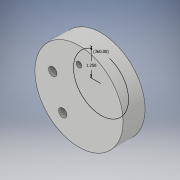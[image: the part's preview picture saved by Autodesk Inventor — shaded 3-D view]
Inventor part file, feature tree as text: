
AUTODESK INVENTOR PART (.ipt)
format: ipt  version: 2018 (Build 220112000, 112)  size: 127,488 bytes
history: native  units: in
note: dims shown in document units (in); Inventor stores cm internally (conversion verified against a paired STEP export)
features: hole x4, sketch x2, extrude x1
ambient origin geometry x8: Origin, YZ Plane, XZ Plane, XY Plane, X Axis, Y Axis, Z Axis, Center Point
bodies: Body1 (feature_tree)
feature tree (7):
  extrude  "Extrusion2"  Depth=2.5in
  sketch  "Sketch4"  dims[d9=1.0in d10=0.0in d12=1.25in d13=1.9685in d15=360.0deg d17=0.25in d18=0.75in d19=0.375in d20=0.25in d21=0.5635in d22=1.25in d23=0.8108in d24=0.375in d25=0.75in d26=0.75in d27=0.25in d28=0.5635in d29=1.25in d30=0.8108in d31=0.196in d32=0.5in d33=0.375in d34=0.25in d35=0.5635in d36=0.75in d37=0.0in d38=0.531in d39=0.5in d40=0.375in d41=0.25in d42=0.5635in d43=0.75in d44=0.0in d11=1.0in]
  hole  "Hole1"  [1 undecoded]
  hole  "Hole2"  [1 undecoded]
  hole  "Hole3"  [1 undecoded]
  hole  "Hole4"  [1 undecoded]
  sketch  "Sketch1"  dims[d0=4.0in d1=2.5in]
note: 4 required parameter values undecoded (feature->parameter linkage not recoverable at this tier; creation-order binding heuristic only, values carry confidence <= 0.55)
